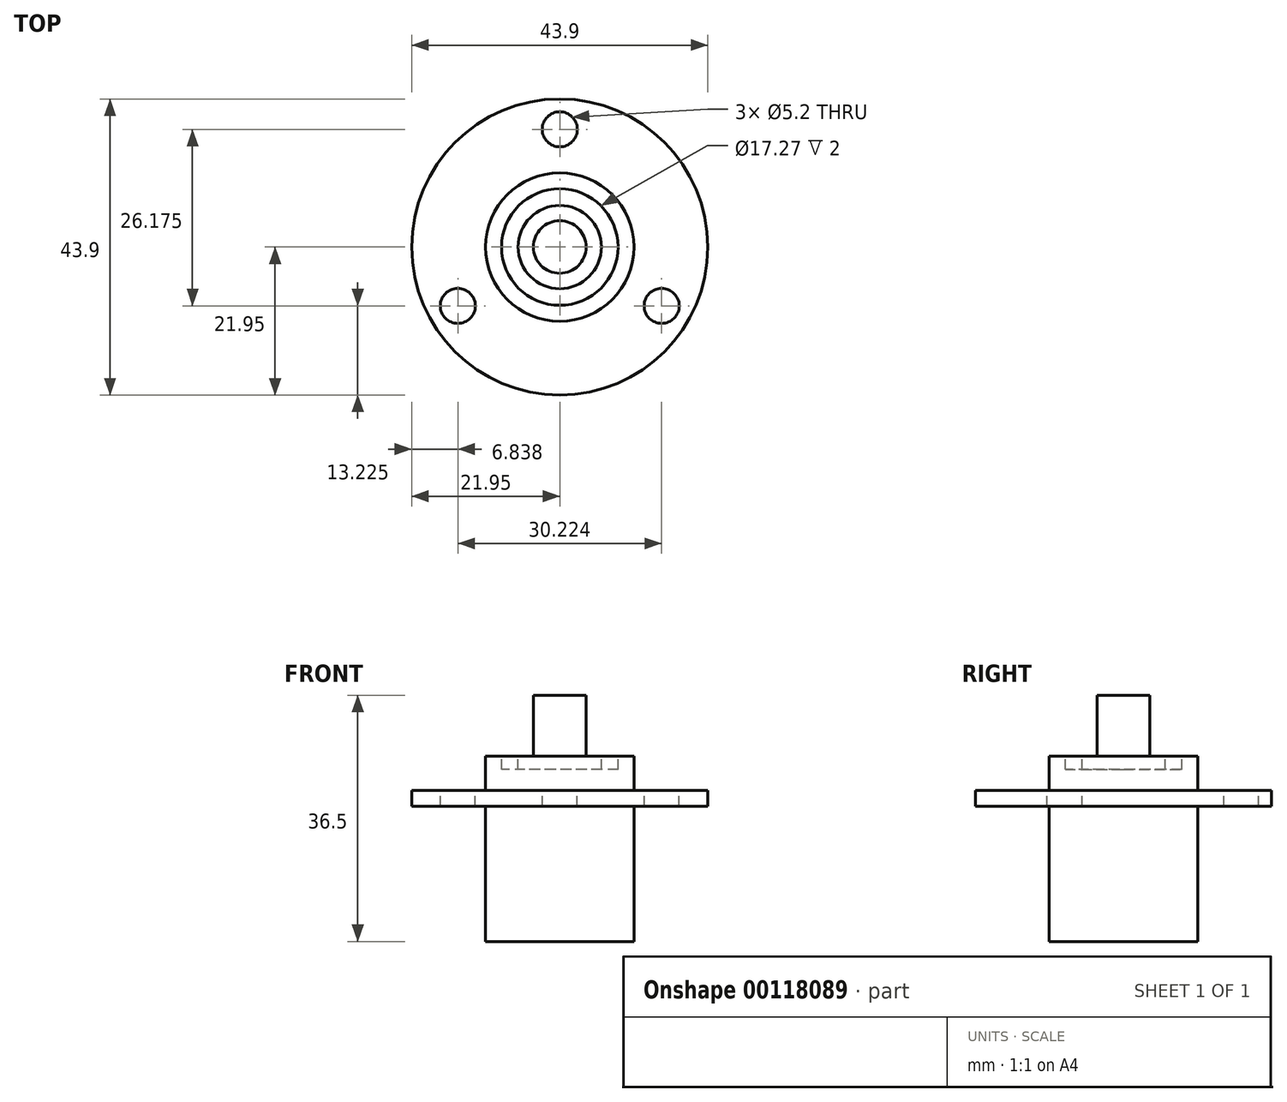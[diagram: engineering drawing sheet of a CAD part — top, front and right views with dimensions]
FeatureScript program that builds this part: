
annotation { "Feature Type Name" : "Feature", "Feature Type Description" : "" }
export const myFeature = defineFeature(function(context is Context, id is Id, definition is map)
    precondition{}
    {
        {
            var Q0;
            Q0=qCreatedBy(makeId("Front.planeOp"),FACE);
            var sketch = newSketch(context, id + "F0", { "sketchPlane" : qUnion([Q0])});
            skLineSegment(sketch, "E0", {"start": v(-11, 7.43) * mm, "end": v(-11, 2.35) * mm});
            skLineSegment(sketch, "E1", {"start": v(-11, 2.35) * mm, "end": v(-21.95, 2.35) * mm});
            skLineSegment(sketch, "E2", {"start": v(-21.95, 2.35) * mm, "end": v(-21.95, 0) * mm});
            skLineSegment(sketch, "E3", {"start": v(-21.95, 0) * mm, "end": v(-11, 0) * mm});
            skLineSegment(sketch, "E4", {"start": v(-11, 0) * mm, "end": v(-11, -20.07) * mm});
            skLineSegment(sketch, "E5", {"start": v(-11, -20.07) * mm, "end": v(0, -20.07) * mm});
            skLineSegment(sketch, "E6", {"start": v(-11, 7.43) * mm, "end": v(-3.9, 7.43) * mm});
            skLineSegment(sketch, "E7", {"start": v(-3.9, 7.43) * mm, "end": v(-3.9, 16.43) * mm});
            skLineSegment(sketch, "E8", {"start": v(-3.9, 16.43) * mm, "end": v(0, 16.43) * mm});
            skLineSegment(sketch, "E9", {"start": v(0, 16.43) * mm, "end": v(0, -20.07) * mm});
            skSolve(sketch);
        }
        {
            var Q0;
            Q0=makeQuery(id+"F0.imprint","IMPRINT",FACE,{"disambiguationData":[TD([[makeQuery(id+"F0.imprint","IMPRINT",EDGE,{"derivedFrom":sQuery(id+"F0.wireOp",EDGE,"E0")}),1.0]])]});
            var Q1;
            Q1=sQuery(id+"F0.wireOp",EDGE,"E9");
            revolve(context, id + "F1", {"entities" : qUnion([Q0]), "axis" : qUnion([Q1]), "revolveType" : RevolveType.FULL});
        }
        {
            var Q0;
            Q0=makeQuery(id+"F1.opRevolve","SWEPT_FACE",FACE,{"disambiguationData":[OSD([sQuery(id+"F0.wireOp",EDGE,"E1")])]});
            var sketch = newSketch(context, id + "F2", { "sketchPlane" : qUnion([Q0])});
            skCircle(sketch, "E10", {"center": v(0, 0) * mm, "radius": 17.45 * mm, "construction": true});
            skLineSegment(sketch, "E11", {"start": v(0, 0) * mm, "end": v(0, 17.45) * mm, "construction": true});
            skLineSegment(sketch, "E12", {"start": v(0, 0) * mm, "end": v(15.11, -8.72) * mm, "construction": true});
            skLineSegment(sketch, "E13", {"start": v(0, 0) * mm, "end": v(-15.11, -8.73) * mm, "construction": true});
            skCircle(sketch, "E14", {"center": v(0, 17.45) * mm, "radius": 2.6 * mm});
            skCircle(sketch, "E15", {"center": v(-15.11, -8.73) * mm, "radius": 2.6 * mm});
            skCircle(sketch, "E16", {"center": v(15.11, -8.72) * mm, "radius": 2.6 * mm});
            skSolve(sketch);
        }
        {
            var Q0;
            Q0=makeQuery(id+"F2.imprint","IMPRINT",FACE,{"disambiguationData":[TD([[makeQuery(id+"F2.imprint","IMPRINT",EDGE,{"derivedFrom":sQuery(id+"F2.wireOp",EDGE,"E14")}),1.0]])]});
            var Q1;
            Q1=makeQuery(id+"F2.imprint","IMPRINT",FACE,{"disambiguationData":[TD([[makeQuery(id+"F2.imprint","IMPRINT",EDGE,{"derivedFrom":sQuery(id+"F2.wireOp",EDGE,"E16")}),1.0]])]});
            var Q2;
            Q2=makeQuery(id+"F2.imprint","IMPRINT",FACE,{"disambiguationData":[TD([[makeQuery(id+"F2.imprint","IMPRINT",EDGE,{"derivedFrom":sQuery(id+"F2.wireOp",EDGE,"E15")}),1.0]])]});
            extrude(context, id + "F3", {"entities" : qUnion([Q0, Q1, Q2]), "operationType" : NewBodyOperationType.REMOVE, "endBound" : BoundingType.UP_TO_NEXT, "oppositeDirection" : true, "depth" : 25 * mm});
        }
        {
            var Q0;
            Q0=makeQuery(id+"F1.opRevolve","SWEPT_FACE",FACE,{"disambiguationData":[OSD([sQuery(id+"F0.wireOp",EDGE,"E6")])]});
            var sketch = newSketch(context, id + "F4", { "sketchPlane" : qUnion([Q0])});
            skCircle(sketch, "E17", {"center": v(0, 0) * mm, "radius": 6.17 * mm});
            skCircle(sketch, "E18", {"center": v(0, 0) * mm, "radius": 8.64 * mm});
            skSolve(sketch);
        }
        {
            var Q0;
            Q0=makeQuery(id+"F4.imprint","IMPRINT",FACE,{"disambiguationData":[TD([[makeQuery(id+"F4.imprint","IMPRINT",EDGE,{"derivedFrom":sQuery(id+"F4.wireOp",EDGE,"E17")}),-1.0]])]});
            extrude(context, id + "F5", {"entities" : qUnion([Q0]), "operationType" : NewBodyOperationType.REMOVE, "oppositeDirection" : true, "depth" : 2 * mm});
        }
    });
